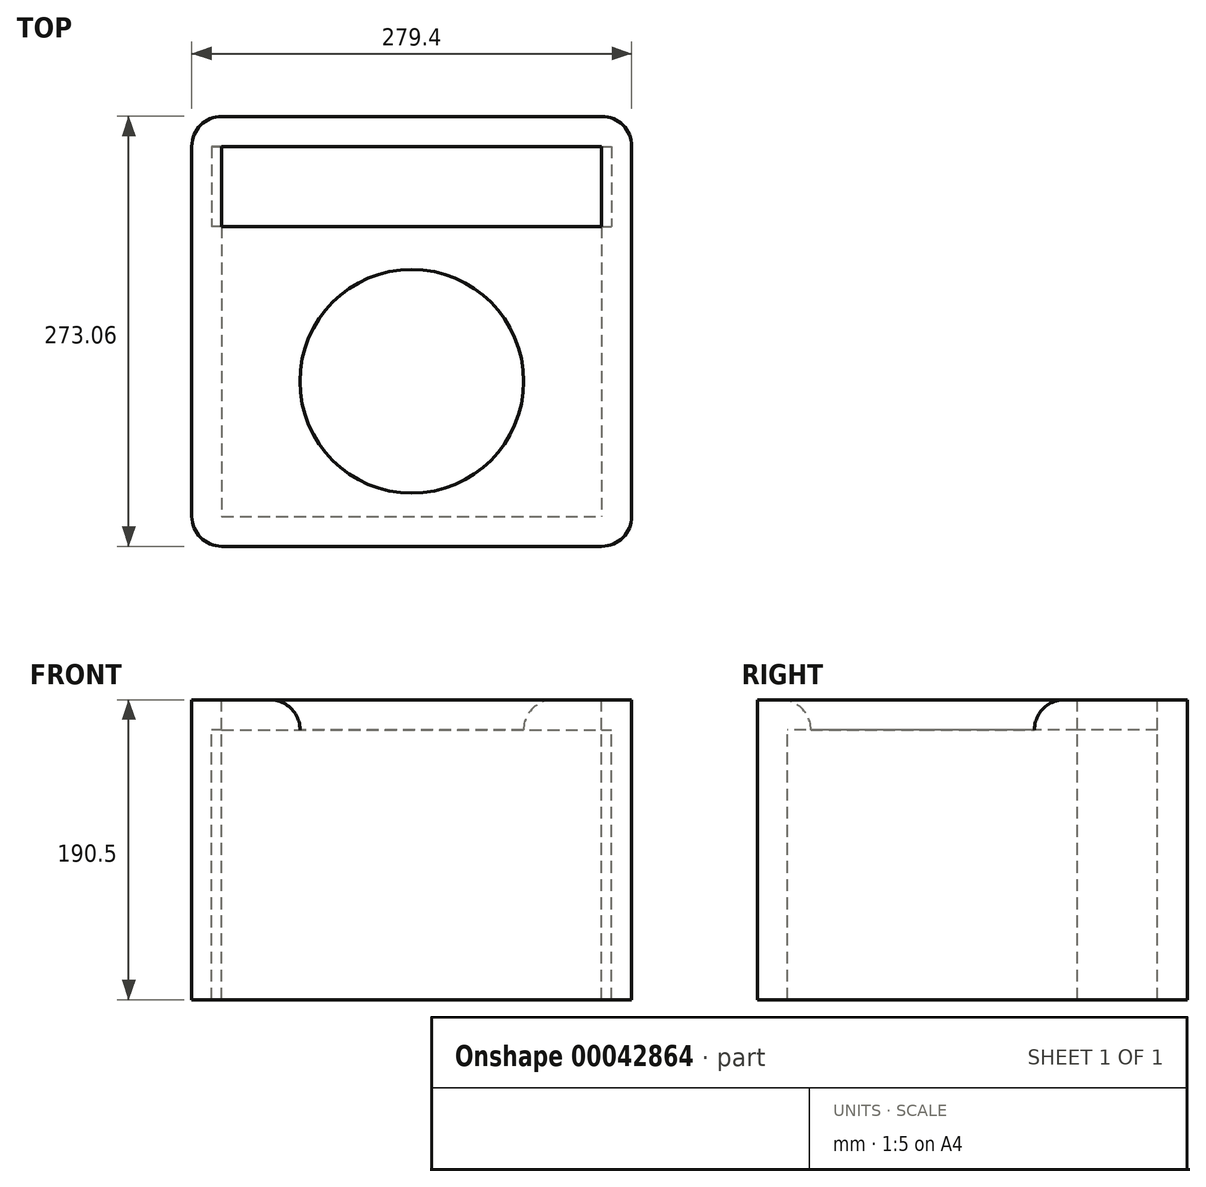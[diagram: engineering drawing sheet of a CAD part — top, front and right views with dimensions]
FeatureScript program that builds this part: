
annotation { "Feature Type Name" : "Feature", "Feature Type Description" : "" }
export const myFeature = defineFeature(function(context is Context, id is Id, definition is map)
    precondition{}
    {
        {
            var Q0;
            Q0=qCreatedBy(makeId("Top.planeOp"),FACE);
            var sketch = newSketch(context, id + "F0", { "sketchPlane" : qUnion([Q0])});
            skLineSegment(sketch, "E0.rect.bottom", {"start": v(120.65, -136.53) * mm, "end": v(-120.65, -136.53) * mm});
            skLineSegment(sketch, "E0.rect.top", {"start": v(120.65, 136.53) * mm, "end": v(-120.65, 136.52) * mm});
            skLineSegment(sketch, "E0.rect.left", {"start": v(139.7, -117.48) * mm, "end": v(139.7, 117.48) * mm});
            skLineSegment(sketch, "E0.rect.right", {"start": v(-139.7, -117.48) * mm, "end": v(-139.7, 117.47) * mm});
            skPoint(sketch, "E0.rect.middle", {"position": v(0, 0) * mm});
            skLineSegment(sketch, "E1", {"start": v(-139.7, 117.47) * mm, "end": v(139.7, 117.48) * mm});
            skLineSegment(sketch, "E2.rect.bottom", {"start": v(127, 66.67) * mm, "end": v(-127, 66.67) * mm});
            skLineSegment(sketch, "E2.rect.top", {"start": v(127, 117.48) * mm, "end": v(-127, 117.47) * mm});
            skLineSegment(sketch, "E2.rect.left", {"start": v(127, 66.68) * mm, "end": v(127, 117.48) * mm});
            skLineSegment(sketch, "E2.rect.right", {"start": v(-127, 66.67) * mm, "end": v(-127, 117.47) * mm});
            skPoint(sketch, "E2.rect.middle", {"position": v(0, 92.08) * mm});
            skLineSegment(sketch, "E3", {"start": v(-120.65, 66.67) * mm, "end": v(-120.65, -117.48) * mm});
            skLineSegment(sketch, "E4", {"start": v(120.65, 66.67) * mm, "end": v(120.65, -117.48) * mm});
            skLineSegment(sketch, "E5", {"start": v(-120.65, -117.48) * mm, "end": v(120.65, -117.48) * mm});
            skCircle(sketch, "E6", {"center": v(0, -31.75) * mm, "radius": 71 * mm});
            skPoint(sketch, "E7.visualSharp", {"position": v(-139.7, 136.52) * mm});
            skArc(sketch, "E7.filletArc", {"start": v(-120.65, 136.53) * mm, "mid": v(-134.12, 130.95) * mm, "end": v(-139.7, 117.47) * mm});
            skPoint(sketch, "E8.visualSharp", {"position": v(139.7, 136.53) * mm});
            skArc(sketch, "E8.filletArc", {"start": v(139.7, 117.48) * mm, "mid": v(134.12, 130.95) * mm, "end": v(120.65, 136.53) * mm});
            skPoint(sketch, "E9.visualSharp", {"position": v(139.7, -136.52) * mm});
            skArc(sketch, "E9.filletArc", {"start": v(120.65, -136.53) * mm, "mid": v(134.12, -130.95) * mm, "end": v(139.7, -117.48) * mm});
            skPoint(sketch, "E10.visualSharp", {"position": v(-139.7, -136.53) * mm});
            skArc(sketch, "E10.filletArc", {"start": v(-139.7, -117.48) * mm, "mid": v(-134.12, -130.95) * mm, "end": v(-120.65, -136.53) * mm});
            skCircle(sketch, "E11", {"center": v(-101.6, 92.07) * mm, "radius": 9.53 * mm});
            skCircle(sketch, "E12", {"center": v(-60.96, 92.07) * mm, "radius": 9.53 * mm});
            skCircle(sketch, "E13", {"center": v(101.6, 92.08) * mm, "radius": 4.76 * mm});
            skCircle(sketch, "E14", {"center": v(60.96, 92.08) * mm, "radius": 4.76 * mm});
            skCircle(sketch, "E15", {"center": v(-20.32, 92.07) * mm, "radius": 9.53 * mm});
            skCircle(sketch, "E16", {"center": v(20.32, 92.08) * mm, "radius": 9.53 * mm});
            skLineSegment(sketch, "E17", {"start": v(-120.65, 111.13) * mm, "end": v(120.65, 111.13) * mm});
            skLineSegment(sketch, "E18", {"start": v(120.65, 111.13) * mm, "end": v(120.65, 73.02) * mm});
            skLineSegment(sketch, "E19", {"start": v(120.65, 73.02) * mm, "end": v(-120.65, 73.03) * mm});
            skLineSegment(sketch, "E20", {"start": v(-120.65, 73.03) * mm, "end": v(-120.65, 111.13) * mm});
            skSolve(sketch);
        }
        {
            var Q0;
            Q0=makeQuery(id+"F0.imprint","IMPRINT",FACE,{"disambiguationData":[TD([[makeQuery(id+"F0.imprint","IMPRINT",EDGE,{"derivedFrom":sQuery(id+"F0.wireOp",EDGE,"E0.rect.bottom")}),-1.0]])]});
            var Q1;
            Q1=makeQuery(id+"F0.imprint","IMPRINT",FACE,{"disambiguationData":[TD([[makeQuery(id+"F0.imprint","IMPRINT",EDGE,{"derivedFrom":sQuery(id+"F0.wireOp",EDGE,"E0.rect.top")}),1.0]])]});
            extrude(context, id + "F1", {"entities" : qUnion([Q0, Q1]), "oppositeDirection" : true, "depth" : 190.5 * mm});
        }
        {
            var Q0;
            Q0=makeQuery(id+"F1.opExtrude","SWEPT_FACE",FACE,{"disambiguationData":[OSD([sQuery(id+"F0.wireOp",EDGE,"E2.rect.left")])]});
            var sketch = newSketch(context, id + "F2", { "sketchPlane" : qUnion([Q0])});
            skLineSegment(sketch, "E21", {"start": v(-117.48, -19.05) * mm, "end": v(-66.67, -19.05) * mm});
            skSolve(sketch);
        }
        {
            var Q0;
            {var subQ2=sQuery(id+"F2.wireOp",EDGE,"E21");Q0=makeQuery(id+"F2.imprint","IMPRINT",FACE,{"disambiguationData":[TD([[makeQuery(id+"F2.imprint","IMPRINT",EDGE,{"derivedFrom":subQ2}),1.0]])]});}
            extrude(context, id + "F3", {"entities" : qUnion([Q0]), "operationType" : NewBodyOperationType.ADD, "depth" : 6.35 * mm});
        }
        {
            var Q0;
            Q0=makeQuery(id+"F1.opExtrude","SWEPT_FACE",FACE,{"disambiguationData":[OSD([sQuery(id+"F0.wireOp",EDGE,"E2.rect.right")])]});
            var sketch = newSketch(context, id + "F4", { "sketchPlane" : qUnion([Q0])});
            skLineSegment(sketch, "E22", {"start": v(117.47, -19.05) * mm, "end": v(66.67, -19.05) * mm});
            skSolve(sketch);
        }
        {
            var Q0;
            {var subQ2=sQuery(id+"F4.wireOp",EDGE,"E22");Q0=makeQuery(id+"F4.imprint","IMPRINT",FACE,{"disambiguationData":[TD([[makeQuery(id+"F4.imprint","IMPRINT",EDGE,{"derivedFrom":subQ2}),-1.0]])]});}
            extrude(context, id + "F5", {"entities" : qUnion([Q0]), "operationType" : NewBodyOperationType.ADD, "depth" : 6.35 * mm});
        }
        {
            var Q0;
            {var subQ0=sQuery(id+"F0.wireOp",EDGE,"E3");Q0=makeQuery(id+"F0.imprint","IMPRINT",FACE,{"disambiguationData":[TD([[makeQuery(id+"F0.imprint","IMPRINT",EDGE,{"derivedFrom":subQ0}),1.0]])]});}
            var Q1;
            Q1=makeQuery(id+"F0.imprint","IMPRINT",FACE,{"disambiguationData":[TD([[makeQuery(id+"F0.imprint","IMPRINT",EDGE,{"derivedFrom":sQuery(id+"F0.wireOp",EDGE,"E2.rect.top")}),1.0]])]});
            extrude(context, id + "F6", {"entities" : qUnion([Q0, Q1]), "operationType" : NewBodyOperationType.ADD, "oppositeDirection" : true, "depth" : 19.05 * mm});
        }
        {
            var Q0;
            Q0=makeQuery(id+"F6.opExtrude","CAP_EDGE",EDGE,{"disambiguationData":[OSD([sQuery(id+"F0.wireOp",EDGE,"E6")])],"isStart":true});
            fillet(context, id + "F7", {"entities" : qUnion([Q0]), "radius" : 19.05 * mm, "tangentPropagation" : true, "allowEdgeOverflow" : false});
        }
    });
